# Revit family: Electronics_Masking-Loudspeakers_Biamp_Cambridge_Sound-Masking-Loudspeakers_DS1339_1357__
name_source: partatom
category: Communication Devices
units: mm (PartAtom-declared; Revit-internal decimal feet)

## family parameters
Cut with Voids When Loaded = No
Host = Face
Maintain Annotation Orientation = No
OmniClass Number = 23.85.10.11.11
OmniClass Title = Sound and Signal Devices
Part Type = Normal
Room Calculation Point = No
Round Connector Dimension = Use Diameter
Shared = No

## types (4) — shared parameters
Cabling = 2 conductor 20AWG
Certifications = UL 1480A and UL 2043
Color = White or black
Connections = 2- Wire Pigtail
Default Elevation = 48 "
Diameter = 8.5 "
Driver Diameter = 5.25”
Enclosure = Ported
Enclosure material = Cold rolled steel plate, thickness: 1 mm, powder coated
Frequency Response = -10dB down: 125Hz to 10,000Hz
Height = 5 "
Loudspeaker Type = 5.25” full range paper cone driver with one-inch voice coil diameter. 8 Ohm
Manufacturer = Biamp
Nominal Dispersion = 160° H x 165° V
Nominal Impedance = 8 Ohms
Product Documentation Link = https://downloads.biamp.com
Product Page URL = https://www.biamp.com
Product data url = https://www.bimobject.com
Sensitivity = 2.83 Volts at 1 meter on Axis: 91.9
Shipping Dimensions = 22” x 22” x 7” (4-pack)
Shipping Weight = 24.20 lbf
Transformer Taps = 1/8,1/4, 1/2,1,2,4 watts
URL = https://www.biamp.com
Weight = 4.20 lbf

## per-type parameters (varying)
| type | Description | Housing Material | Model |
| DS1357 White | Dynasound® DS1357 Sound Masking, Paging, and Music Speaker for 8 Ohm Systems | Biamp - Plastic - White | DS1357 |
| DS1357 Black | Dynasound® DS1357 Sound Masking, Paging, and Music Speaker for 8 Ohm Systems | Biamp - Plastic - Black | DS1357 |
| DS1339 White | Dynasound® DS1339 Sound Masking, Paging, and Music Speaker for 70.7 Volt Systems | Biamp - Plastic - White | DS1339 |
| DS1339 Black | Dynasound® DS1339 Sound Masking, Paging, and Music Speaker for 70.7 Volt Systems | Biamp - Plastic - Black | DS1339 |

## geometry (parser evidence)
native form markers: Sweep x2
no freeform markers — native parametric forms only
